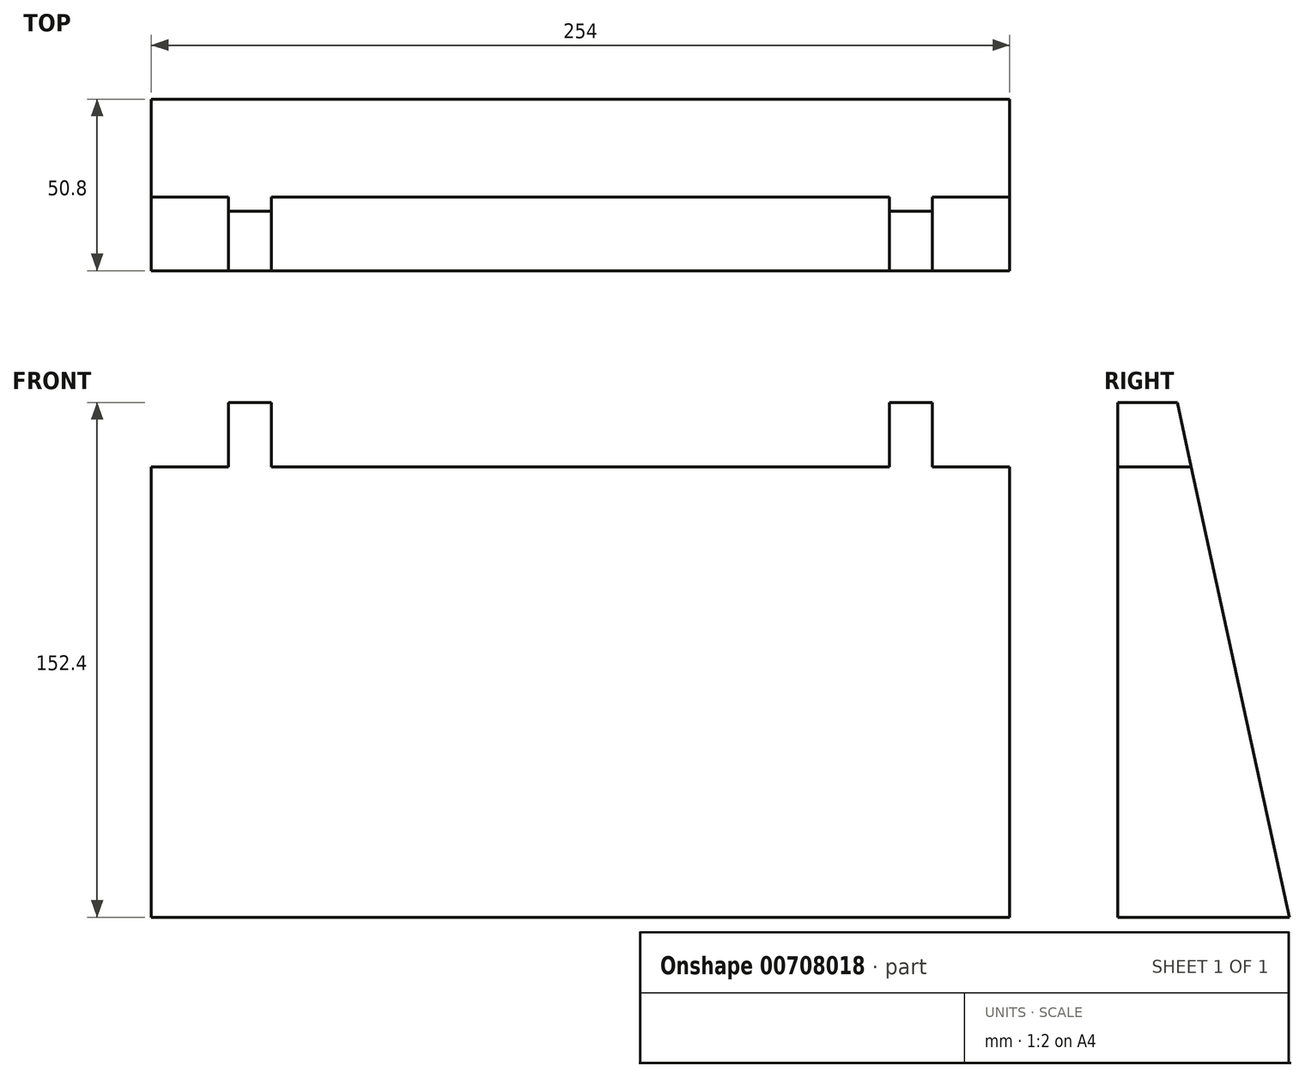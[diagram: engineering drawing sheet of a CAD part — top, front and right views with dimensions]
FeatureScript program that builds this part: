
annotation { "Feature Type Name" : "Feature", "Feature Type Description" : "" }
export const myFeature = defineFeature(function(context is Context, id is Id, definition is map)
    precondition{}
    {
        {
            var Q0;
            Q0=qCreatedBy(makeId("Front.planeOp"),FACE);
            var sketch = newSketch(context, id + "F0", { "sketchPlane" : qUnion([Q0])});
            skLineSegment(sketch, "E0.bottom", {"start": v(-127, -76.2) * mm, "end": v(127, -76.2) * mm});
            skLineSegment(sketch, "E0.top", {"start": v(-127, 76.2) * mm, "end": v(127, 76.2) * mm});
            skLineSegment(sketch, "E0.left", {"start": v(-127, -76.2) * mm, "end": v(-127, 76.2) * mm});
            skLineSegment(sketch, "E0.right", {"start": v(127, -76.2) * mm, "end": v(127, 76.2) * mm});
            skPoint(sketch, "E0.middle", {"position": v(0, 0) * mm});
            skSolve(sketch);
        }
        {
            var Q0;
            Q0=makeQuery(id+"F0.imprint","IMPRINT",FACE,{"disambiguationData":[TD([[makeQuery(id+"F0.imprint","IMPRINT",EDGE,{"derivedFrom":sQuery(id+"F0.wireOp",EDGE,"E0.bottom")}),1.0]])]});
            extrude(context, id + "F1", {"entities" : qUnion([Q0]), "depth" : 50.8 * mm, "offsetDistance" : 25.4 * mm});
        }
        {
            var Q0;
            Q0=makeQuery(id+"F1.opExtrude","SWEPT_FACE",FACE,{"disambiguationData":[OSD([sQuery(id+"F0.wireOp",EDGE,"E0.right")])]});
            var sketch = newSketch(context, id + "F2", { "sketchPlane" : qUnion([Q0])});
            skLineSegment(sketch, "E1", {"start": v(0, -76.2) * mm, "end": v(-33.23, 76.2) * mm});
            skLineSegment(sketch, "E2", {"start": v(-33.23, 76.2) * mm, "end": v(0, 76.2) * mm});
            skLineSegment(sketch, "E3", {"start": v(0, 76.2) * mm, "end": v(0, -76.2) * mm});
            skSolve(sketch);
        }
        {
            var Q0;
            Q0=makeQuery(id+"F2.imprint","IMPRINT",FACE,{"disambiguationData":[TD([[makeQuery(id+"F2.imprint","IMPRINT",EDGE,{"derivedFrom":sQuery(id+"F2.wireOp",EDGE,"E1")}),-1.0]])]});
            extrude(context, id + "F3", {"entities" : qUnion([Q0]), "operationType" : NewBodyOperationType.REMOVE, "endBound" : BoundingType.THROUGH_ALL, "oppositeDirection" : true, "depth" : 25.4 * mm, "offsetDistance" : 25.4 * mm});
        }
        {
            var Q0;
            Q0=makeQuery(id+"F1.opExtrude","CAP_FACE",FACE,{"disambiguationData":[OSD([sQuery(id+"F0.wireOp",EDGE,"E0.bottom"),sQuery(id+"F0.wireOp",EDGE,"E0.top"),sQuery(id+"F0.wireOp",EDGE,"E0.left"),sQuery(id+"F0.wireOp",EDGE,"E0.right")])],"isStart":false});
            var sketch = newSketch(context, id + "F4", { "sketchPlane" : qUnion([Q0])});
            skLineSegment(sketch, "E4", {"start": v(-127, 57.15) * mm, "end": v(-104.14, 57.15) * mm});
            skLineSegment(sketch, "E5", {"start": v(-104.14, 57.15) * mm, "end": v(-104.14, 76.2) * mm});
            skLineSegment(sketch, "E6", {"start": v(-104.14, 76.2) * mm, "end": v(-127, 76.2) * mm});
            skLineSegment(sketch, "E7", {"start": v(-127, 76.2) * mm, "end": v(-127, 57.15) * mm});
            skLineSegment(sketch, "E8", {"start": v(127, 76.2) * mm, "end": v(104.14, 76.2) * mm});
            skLineSegment(sketch, "E9", {"start": v(104.14, 76.2) * mm, "end": v(104.14, 57.15) * mm});
            skLineSegment(sketch, "E10", {"start": v(104.14, 57.15) * mm, "end": v(127, 57.15) * mm});
            skLineSegment(sketch, "E11", {"start": v(127, 57.15) * mm, "end": v(127, 76.2) * mm});
            skLineSegment(sketch, "E12", {"start": v(91.44, 76.2) * mm, "end": v(91.44, 57.15) * mm});
            skLineSegment(sketch, "E13", {"start": v(91.44, 57.15) * mm, "end": v(-91.44, 57.15) * mm});
            skLineSegment(sketch, "E14", {"start": v(-91.44, 57.15) * mm, "end": v(-91.44, 76.2) * mm});
            skLineSegment(sketch, "E15", {"start": v(-91.44, 76.2) * mm, "end": v(91.44, 76.2) * mm});
            skSolve(sketch);
        }
        {
            var Q0;
            Q0=makeQuery(id+"F4.imprint","IMPRINT",FACE,{"disambiguationData":[TD([[makeQuery(id+"F4.imprint","IMPRINT",EDGE,{"derivedFrom":sQuery(id+"F4.wireOp",EDGE,"E4")}),1.0]])]});
            var Q1;
            Q1=makeQuery(id+"F4.imprint","IMPRINT",FACE,{"disambiguationData":[TD([[makeQuery(id+"F4.imprint","IMPRINT",EDGE,{"derivedFrom":sQuery(id+"F4.wireOp",EDGE,"E12")}),-1.0]])]});
            var Q2;
            Q2=makeQuery(id+"F4.imprint","IMPRINT",FACE,{"disambiguationData":[TD([[makeQuery(id+"F4.imprint","IMPRINT",EDGE,{"derivedFrom":sQuery(id+"F4.wireOp",EDGE,"E8")}),-1.0]])]});
            extrude(context, id + "F5", {"entities" : qUnion([Q0, Q1, Q2]), "operationType" : NewBodyOperationType.REMOVE, "endBound" : BoundingType.THROUGH_ALL, "oppositeDirection" : true, "depth" : 25.4 * mm, "offsetDistance" : 25.4 * mm});
        }
    });
